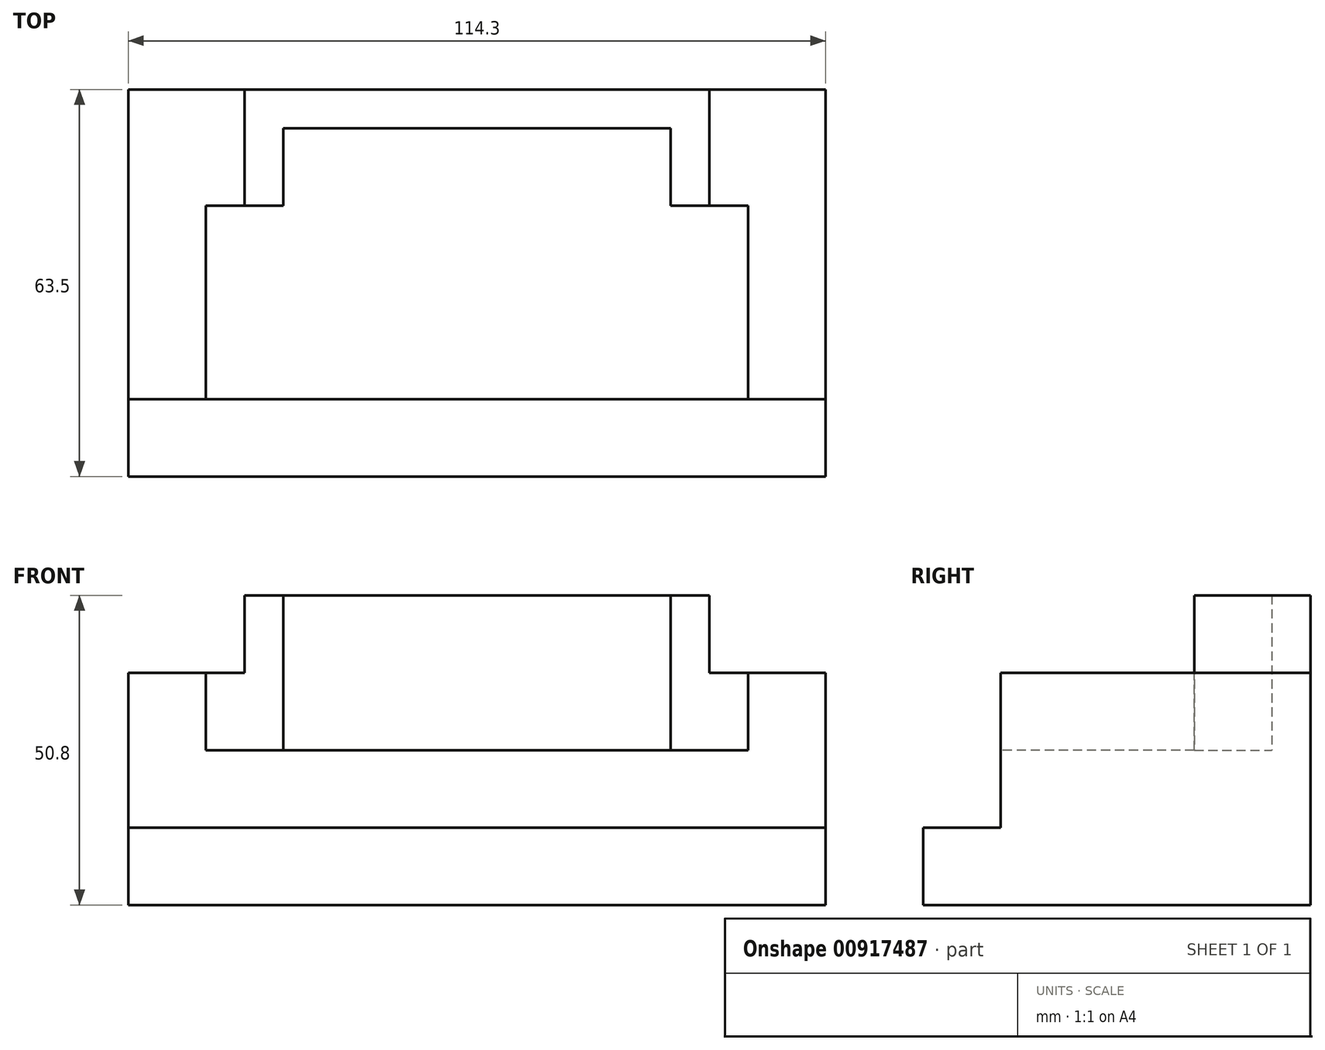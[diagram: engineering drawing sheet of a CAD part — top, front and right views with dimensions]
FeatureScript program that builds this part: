
annotation { "Feature Type Name" : "Feature", "Feature Type Description" : "" }
export const myFeature = defineFeature(function(context is Context, id is Id, definition is map)
    precondition{}
    {
        {
            var Q0;
            Q0=qCreatedBy(makeId("Top.planeOp"),FACE);
            var sketch = newSketch(context, id + "F0", { "sketchPlane" : qUnion([Q0])});
            skLineSegment(sketch, "E0.bottom", {"start": v(-34.77, -21.07) * mm, "end": v(79.53, -21.07) * mm});
            skLineSegment(sketch, "E0.top", {"start": v(-34.77, 42.43) * mm, "end": v(79.53, 42.43) * mm});
            skLineSegment(sketch, "E0.left", {"start": v(-34.77, -21.07) * mm, "end": v(-34.77, 42.43) * mm});
            skLineSegment(sketch, "E0.right", {"start": v(79.53, -21.07) * mm, "end": v(79.53, 42.43) * mm});
            skSolve(sketch);
        }
        {
            var Q0;
            Q0=makeQuery(id+"F0.imprint","IMPRINT",FACE,{"disambiguationData":[TD([[makeQuery(id+"F0.imprint","IMPRINT",EDGE,{"derivedFrom":sQuery(id+"F0.wireOp",EDGE,"E0.bottom")}),1.0]])]});
            extrude(context, id + "F1", {"entities" : qUnion([Q0]), "depth" : 38.1 * mm, "offsetDistance" : 25.4 * mm});
        }
        {
            var Q0;
            Q0=makeQuery(id+"F1.opExtrude","CAP_FACE",FACE,{"disambiguationData":[OSD([sQuery(id+"F0.wireOp",EDGE,"E0.bottom"),sQuery(id+"F0.wireOp",EDGE,"E0.top"),sQuery(id+"F0.wireOp",EDGE,"E0.left"),sQuery(id+"F0.wireOp",EDGE,"E0.right")])],"isStart":false});
            var sketch = newSketch(context, id + "F2", { "sketchPlane" : qUnion([Q0])});
            skLineSegment(sketch, "E1.bottom", {"start": v(-15.72, 23.38) * mm, "end": v(-9.37, 23.38) * mm});
            skLineSegment(sketch, "E1.top", {"start": v(-15.72, 42.43) * mm, "end": v(-9.37, 42.43) * mm});
            skLineSegment(sketch, "E1.left", {"start": v(-15.72, 23.38) * mm, "end": v(-15.72, 42.43) * mm});
            skLineSegment(sketch, "E1.right", {"start": v(-9.37, 23.38) * mm, "end": v(-9.37, 42.43) * mm});
            skLineSegment(sketch, "E2.bottom", {"start": v(-9.37, 42.43) * mm, "end": v(54.13, 42.43) * mm});
            skLineSegment(sketch, "E2.top", {"start": v(-9.37, 36.08) * mm, "end": v(54.13, 36.08) * mm});
            skLineSegment(sketch, "E2.left", {"start": v(-9.37, 42.43) * mm, "end": v(-9.37, 36.08) * mm});
            skLineSegment(sketch, "E2.right", {"start": v(54.13, 42.43) * mm, "end": v(54.13, 36.08) * mm});
            skLineSegment(sketch, "E3.bottom", {"start": v(60.48, 42.43) * mm, "end": v(54.13, 42.43) * mm});
            skLineSegment(sketch, "E3.top", {"start": v(60.48, 23.38) * mm, "end": v(54.13, 23.38) * mm});
            skLineSegment(sketch, "E3.left", {"start": v(60.48, 42.43) * mm, "end": v(60.48, 23.38) * mm});
            skLineSegment(sketch, "E3.right", {"start": v(54.13, 42.43) * mm, "end": v(54.13, 23.38) * mm});
            skSolve(sketch);
        }
        {
            var Q0;
            {var subQ1=sQuery(id+"F2.wireOp",EDGE,"E3.bottom");Q0=makeQuery(id+"F2.imprint","IMPRINT",FACE,{"disambiguationData":[TD([[makeQuery(id+"F2.imprint","IMPRINT",EDGE,{"derivedFrom":subQ1}),-1.0]])]});}
            var Q1;
            {var subQ0=sQuery(id+"F2.wireOp",EDGE,"E2.bottom");Q1=makeQuery(id+"F2.imprint","IMPRINT",FACE,{"disambiguationData":[TD([[makeQuery(id+"F2.imprint","IMPRINT",EDGE,{"derivedFrom":subQ0}),-1.0]])]});}
            var Q2;
            Q2=makeQuery(id+"F2.imprint","IMPRINT",FACE,{"disambiguationData":[TD([[makeQuery(id+"F2.imprint","IMPRINT",EDGE,{"derivedFrom":sQuery(id+"F2.wireOp",EDGE,"E1.bottom")}),1.0]])]});
            extrude(context, id + "F3", {"entities" : qUnion([Q0, Q1, Q2]), "operationType" : NewBodyOperationType.ADD, "depth" : 12.7 * mm, "offsetDistance" : 25.4 * mm});
        }
        {
            var Q0;
            Q0=makeQuery(id+"F1.opExtrude","CAP_FACE",FACE,{"disambiguationData":[OSD([sQuery(id+"F0.wireOp",EDGE,"E0.bottom"),sQuery(id+"F0.wireOp",EDGE,"E0.top"),sQuery(id+"F0.wireOp",EDGE,"E0.left"),sQuery(id+"F0.wireOp",EDGE,"E0.right")])],"isStart":false});
            var sketch = newSketch(context, id + "F4", { "sketchPlane" : qUnion([Q0])});
            skLineSegment(sketch, "E4.bottom", {"start": v(-22.07, 23.38) * mm, "end": v(66.83, 23.38) * mm});
            skLineSegment(sketch, "E4.top", {"start": v(-22.07, -8.37) * mm, "end": v(66.83, -8.37) * mm});
            skLineSegment(sketch, "E4.left", {"start": v(-22.07, 23.38) * mm, "end": v(-22.07, -8.37) * mm});
            skLineSegment(sketch, "E4.right", {"start": v(66.83, 23.38) * mm, "end": v(66.83, -8.37) * mm});
            skLineSegment(sketch, "E5", {"start": v(-9.37, 23.38) * mm, "end": v(-9.37, 36.08) * mm});
            skLineSegment(sketch, "E6", {"start": v(-9.37, 36.08) * mm, "end": v(54.13, 36.08) * mm});
            skLineSegment(sketch, "E7", {"start": v(54.13, 36.08) * mm, "end": v(54.13, 23.38) * mm});
            skLineSegment(sketch, "E8", {"start": v(54.13, 23.38) * mm, "end": v(-9.37, 23.38) * mm});
            skSolve(sketch);
        }
        {
            var Q0;
            Q0=makeQuery(id+"F4.imprint","IMPRINT",FACE,{"disambiguationData":[TD([[makeQuery(id+"F4.imprint","IMPRINT",EDGE,{"derivedFrom":sQuery(id+"F4.wireOp",EDGE,"E5")}),-1.0]])]});
            var Q1;
            Q1=makeQuery(id+"F4.imprint","IMPRINT",FACE,{"disambiguationData":[TD([[makeQuery(id+"F4.imprint","IMPRINT",EDGE,{"derivedFrom":sQuery(id+"F4.wireOp",EDGE,"E4.top")}),1.0]])]});
            extrude(context, id + "F5", {"entities" : qUnion([Q0, Q1]), "operationType" : NewBodyOperationType.REMOVE, "oppositeDirection" : true, "depth" : 12.7 * mm, "offsetDistance" : 25.4 * mm});
        }
        {
            var Q0;
            Q0=makeQuery(id+"F1.opExtrude","CAP_FACE",FACE,{"disambiguationData":[OSD([sQuery(id+"F0.wireOp",EDGE,"E0.bottom"),sQuery(id+"F0.wireOp",EDGE,"E0.top"),sQuery(id+"F0.wireOp",EDGE,"E0.left"),sQuery(id+"F0.wireOp",EDGE,"E0.right")])],"isStart":false});
            var sketch = newSketch(context, id + "F6", { "sketchPlane" : qUnion([Q0])});
            skLineSegment(sketch, "E9.bottom", {"start": v(-34.77, -8.37) * mm, "end": v(79.53, -8.37) * mm});
            skLineSegment(sketch, "E9.top", {"start": v(-34.77, -21.07) * mm, "end": v(79.53, -21.07) * mm});
            skLineSegment(sketch, "E9.left", {"start": v(-34.77, -8.37) * mm, "end": v(-34.77, -21.07) * mm});
            skLineSegment(sketch, "E9.right", {"start": v(79.53, -8.37) * mm, "end": v(79.53, -21.07) * mm});
            skSolve(sketch);
        }
        {
            var Q0;
            Q0=makeQuery(id+"F6.imprint","IMPRINT",FACE,{"disambiguationData":[TD([[makeQuery(id+"F6.imprint","IMPRINT",EDGE,{"derivedFrom":sQuery(id+"F6.wireOp",EDGE,"E9.top")}),1.0]])]});
            extrude(context, id + "F7", {"entities" : qUnion([Q0]), "operationType" : NewBodyOperationType.REMOVE, "oppositeDirection" : true, "depth" : 25.4 * mm, "offsetDistance" : 25.4 * mm});
        }
    });
